# Revit family: Haworth_X99_Chair_Guest
name_source: partatom
category: Furniture
revit_build: Autodesk Revit 2018 (Build: 20170223_1515(x64)
units: mm (PartAtom-declared; Revit-internal decimal feet)

## family parameters
Always vertical = Yes
Cut with Voids When Loaded = No
OmniClass Number = 23.40.70.14.64.11
OmniClass Title = Office Furniture
Room Calculation Point = No
Shared = No
Work Plane-Based = No

## types (1)
- X99 Guest Chair
    Assembly Code = E2020200
    Back Cushion = No
    Back Mesh = Yes
    Back Upholstery Finish = Haworth _ Fabric _ Zinger _ Gravel NI-4
    Base Finish = Haworth _ Metal _ Chrome
    Description = Haworth - Chair - X99 - Guest
    Manufacturer = Haworth
    Model = Haworth - Chair - X99 - Guest
    Revision Number = 3
    Seat Finish = Haworth _ Fabric _ Zinger _ Gravel NI-4
    Sustainability Info = http://www.haworth.com
    URL = www.haworth.com
    URL - Product = http://www.haworth.com
    Warranty = http://www.haworth.com

## geometry (parser evidence)
native form markers: Sweep x11
no freeform markers — native parametric forms only
